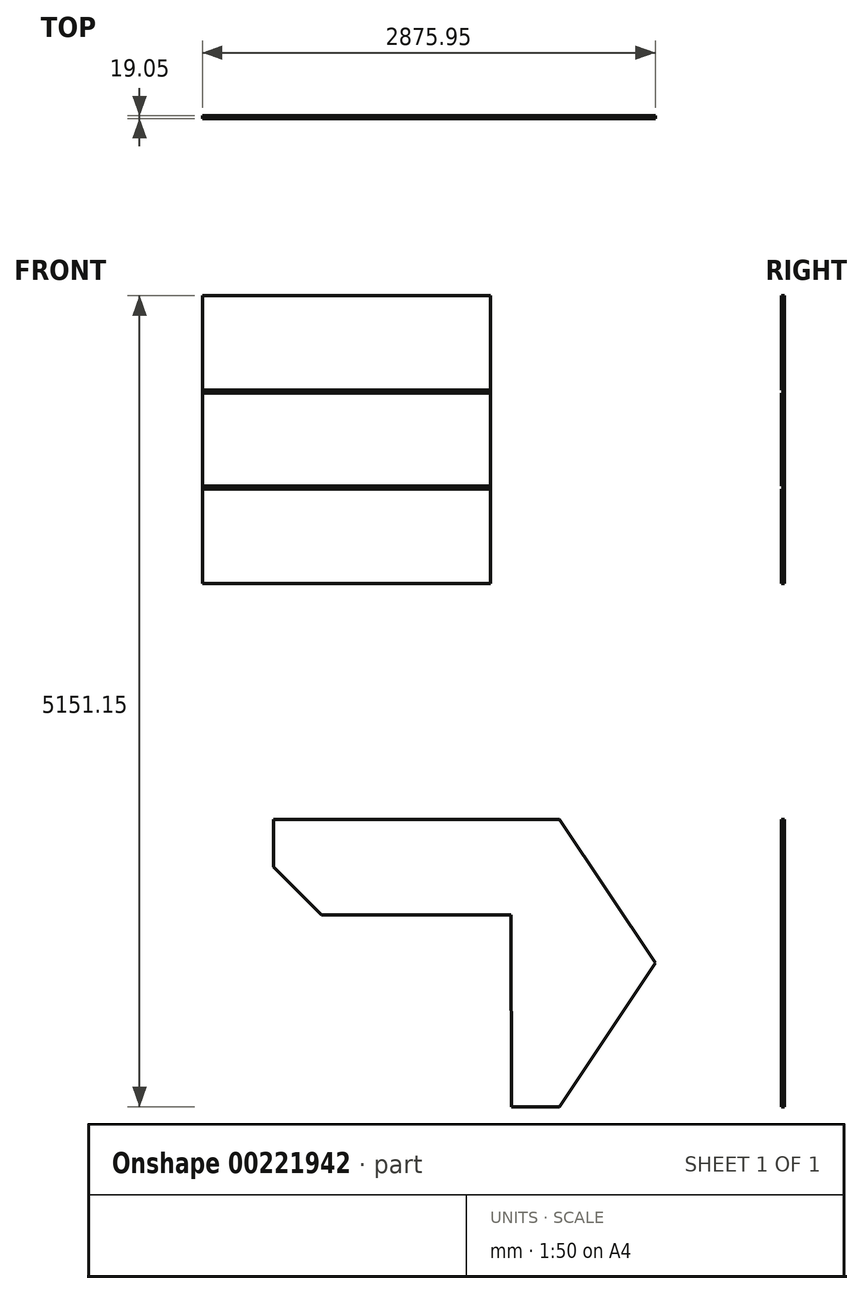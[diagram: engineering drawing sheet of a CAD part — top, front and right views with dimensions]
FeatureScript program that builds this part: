
annotation { "Feature Type Name" : "Feature", "Feature Type Description" : "" }
export const myFeature = defineFeature(function(context is Context, id is Id, definition is map)
    precondition{}
    {
        {
            var Q0;
            Q0=qCreatedBy(makeId("Front.planeOp"),FACE);
            var sketch = newSketch(context, id + "F0", { "sketchPlane" : qUnion([Q0])});
            skLineSegment(sketch, "E0.top", {"start": v(-625.35, -742.19) * mm, "end": v(581.15, -742.19) * mm});
            skLineSegment(sketch, "E0.left", {"start": v(-930.15, -135.76) * mm, "end": v(-930.15, -437.39) * mm});
            skLineSegment(sketch, "E1", {"start": v(888.07, -135.76) * mm, "end": v(1495.55, -1046.99) * mm});
            skLineSegment(sketch, "E2", {"start": v(885.95, -1961.39) * mm, "end": v(1495.55, -1046.99) * mm});
            skLineSegment(sketch, "E3", {"start": v(885.95, -1961.39) * mm, "end": v(581.15, -1961.39) * mm});
            skLineSegment(sketch, "E4", {"start": v(580.25, -742.19) * mm, "end": v(581.15, -1961.39) * mm});
            skLineSegment(sketch, "E5.0", {"start": v(-930.15, -135.76) * mm, "end": v(888.07, -135.76) * mm, "construction": true});
            skLineSegment(sketch, "E6", {"start": v(888.07, -135.76) * mm, "end": v(-930.15, -135.76) * mm});
            skPoint(sketch, "E7.orphan", {"position": v(-930.15, -132.59) * mm});
            skPoint(sketch, "E8.orphan", {"position": v(885.95, -132.59) * mm});
            skLineSegment(sketch, "E9.0", {"start": v(-930.15, -437.39) * mm, "end": v(581.15, -437.39) * mm, "construction": true});
            skLineSegment(sketch, "E10.0", {"start": v(-625.35, -135.76) * mm, "end": v(-625.35, -742.19) * mm, "construction": true});
            skLineSegment(sketch, "E11", {"start": v(-930.15, -437.39) * mm, "end": v(-625.35, -742.19) * mm});
            skPoint(sketch, "E12.orphan", {"position": v(-930.15, -742.19) * mm});
            skSolve(sketch);
        }
        {
            var Q0;
            Q0 = qSketchRegion(id + "F0", true);
            extrude(context, id + "F1", {"entities" : qUnion([Q0]), "depth" : 19.05 * mm});
        }
        {
            var Q0;
            Q0=qCreatedBy(makeId("Front.planeOp"),FACE);
            var sketch = newSketch(context, id + "F2", { "sketchPlane" : qUnion([Q0])});
            skLineSegment(sketch, "E13.bottom", {"start": v(-1380.4, 3189.76) * mm, "end": v(448.4, 3189.76) * mm});
            skLineSegment(sketch, "E13.top", {"start": v(-1380.4, 1360.96) * mm, "end": v(448.4, 1360.96) * mm});
            skLineSegment(sketch, "E13.left", {"start": v(-1380.4, 3189.76) * mm, "end": v(-1380.4, 1360.96) * mm});
            skLineSegment(sketch, "E13.right", {"start": v(448.4, 3189.76) * mm, "end": v(448.4, 1360.96) * mm});
            skLineSegment(sketch, "E14.0", {"start": v(-1380.4, 1961.03) * mm, "end": v(448.4, 1961.03) * mm});
            skLineSegment(sketch, "E15.0", {"start": v(-1380.4, 2570.63) * mm, "end": v(448.4, 2570.63) * mm});
            skLineSegment(sketch, "E16.0", {"start": v(-1380.4, 1980.08) * mm, "end": v(448.4, 1980.08) * mm});
            skLineSegment(sketch, "E17.0", {"start": v(-1380.4, 2589.68) * mm, "end": v(448.4, 2589.68) * mm});
            skSolve(sketch);
        }
        {
            var Q0;
            Q0 = qSketchRegion(id + "F2", true);
            extrude(context, id + "F3", {"entities" : qUnion([Q0]), "depth" : 12.7 * mm});
        }
        {
            var Q0;
            {var subQ0=sQuery(id+"F2.wireOp",EDGE,"E13.bottom");Q0=makeQuery(id+"F2.imprint","IMPRINT",FACE,{"disambiguationData":[TD([[makeQuery(id+"F2.imprint","IMPRINT",EDGE,{"derivedFrom":subQ0}),-1.0]])]});}
            var Q1;
            {var subQ0=sQuery(id+"F2.wireOp",EDGE,"E15.0");Q1=makeQuery(id+"F2.imprint","IMPRINT",FACE,{"disambiguationData":[TD([[makeQuery(id+"F2.imprint","IMPRINT",EDGE,{"derivedFrom":subQ0}),-1.0]])]});}
            var Q2;
            {var subQ0=sQuery(id+"F2.wireOp",EDGE,"E13.top");Q2=makeQuery(id+"F2.imprint","IMPRINT",FACE,{"disambiguationData":[TD([[makeQuery(id+"F2.imprint","IMPRINT",EDGE,{"derivedFrom":subQ0}),1.0]])]});}
            extrude(context, id + "F4", {"entities" : qUnion([Q0, Q1, Q2]), "operationType" : NewBodyOperationType.ADD, "depth" : 19.05 * mm});
        }
        {
            var Q0;
            {var subQ0=sQuery(id+"F2.wireOp",EDGE,"E15.0");var subQ1=sQuery(id+"F2.wireOp",EDGE,"E13.left");var subQ3=sQuery(id+"F2.wireOp",EDGE,"E13.bottom");var subQ5=sQuery(id+"F2.wireOp",EDGE,"E13.right");var subQ6=sQuery(id+"F2.wireOp",EDGE,"E13.top");Q0=makeQuery(id+"F4.boolean.opBoolean","SPLIT",FACE,{"disambiguationData":[TD([makeQuery(id+"F4.opExtrude","SWEPT_FACE",FACE,{"disambiguationData":[OSD([subQ0])]})])],"derivedFrom":makeQuery(id+"F3.opExtrude","CAP_FACE",FACE,{"disambiguationData":[OSD([subQ3,subQ6,subQ1,subQ5])],"isStart":false})});}
            var Q1;
            {var subQ1=sQuery(id+"F2.wireOp",EDGE,"E13.left");var subQ3=sQuery(id+"F2.wireOp",EDGE,"E13.bottom");var subQ5=sQuery(id+"F2.wireOp",EDGE,"E13.right");var subQ6=sQuery(id+"F2.wireOp",EDGE,"E14.0");var subQ7=sQuery(id+"F2.wireOp",EDGE,"E13.top");Q1=makeQuery(id+"F4.boolean.opBoolean","SPLIT",FACE,{"disambiguationData":[TD([makeQuery(id+"F4.opExtrude","SWEPT_FACE",FACE,{"disambiguationData":[OSD([subQ6])]})])],"derivedFrom":makeQuery(id+"F3.opExtrude","CAP_FACE",FACE,{"disambiguationData":[OSD([subQ3,subQ7,subQ1,subQ5])],"isStart":false})});}
            extrude(context, id + "F5", {"entities" : qUnion([Q0, Q1]), "operationType" : NewBodyOperationType.REMOVE, "oppositeDirection" : true, "depth" : 12.7 * mm});
        }
        {
            var Q0;
            {var subQ0=sQuery(id+"F2.wireOp",EDGE,"E14.0");Q0=makeQuery(id+"F2.imprint","IMPRINT",FACE,{"disambiguationData":[TD([[makeQuery(id+"F2.imprint","IMPRINT",EDGE,{"derivedFrom":subQ0}),1.0]])]});}
            var Q1;
            {var subQ0=sQuery(id+"F2.wireOp",EDGE,"E15.0");Q1=makeQuery(id+"F2.imprint","IMPRINT",FACE,{"disambiguationData":[TD([[makeQuery(id+"F2.imprint","IMPRINT",EDGE,{"derivedFrom":subQ0}),1.0]])]});}
            extrude(context, id + "F6", {"entities" : qUnion([Q0, Q1]), "depth" : 3.17 * mm});
        }
    });
